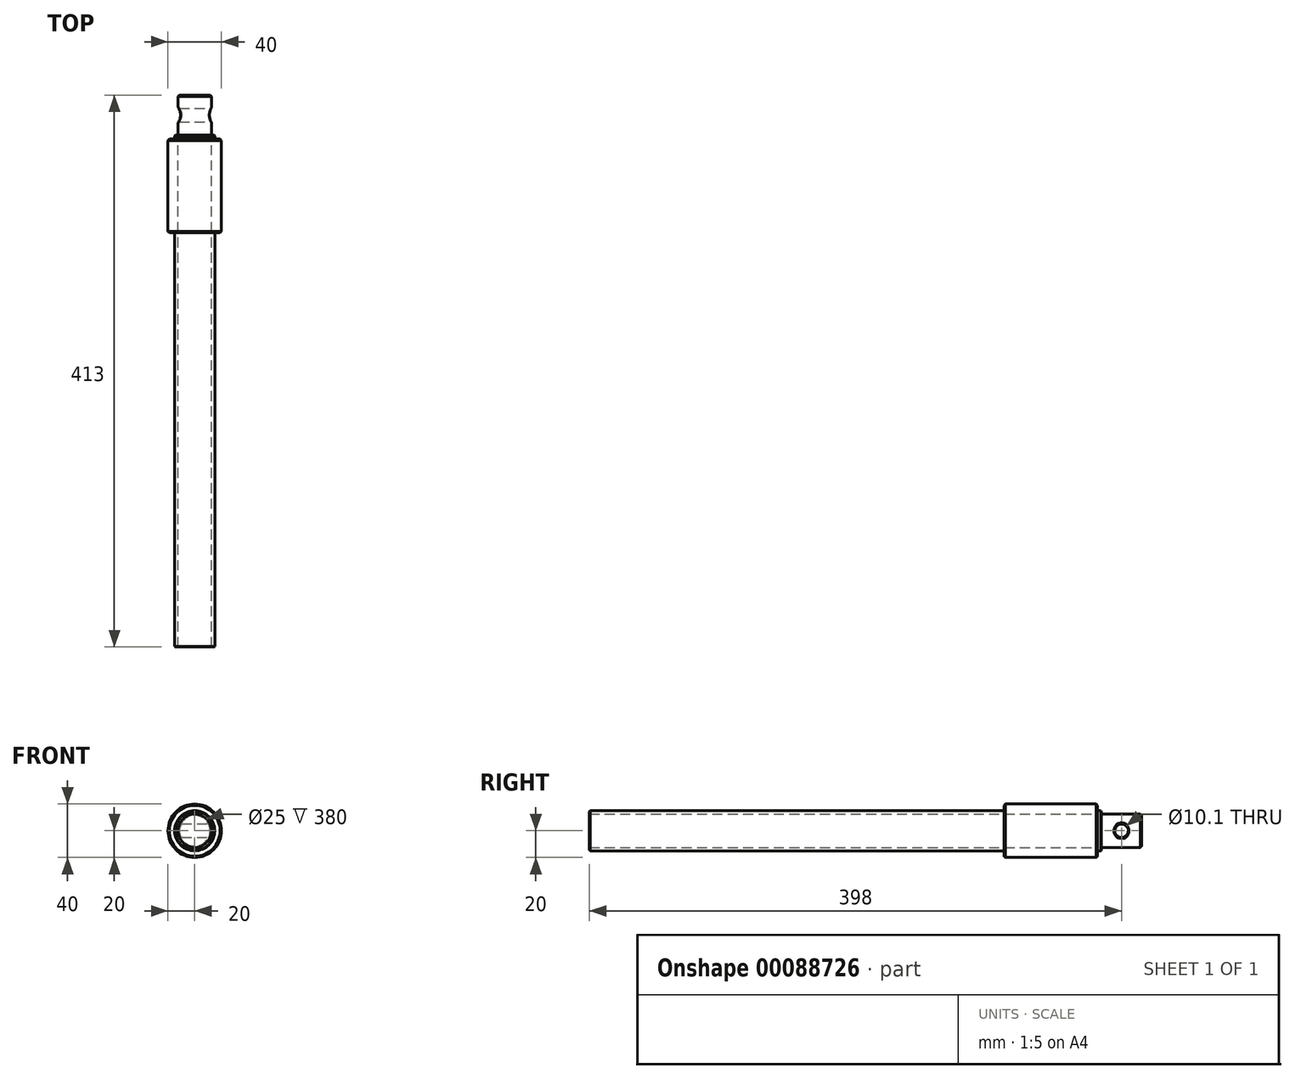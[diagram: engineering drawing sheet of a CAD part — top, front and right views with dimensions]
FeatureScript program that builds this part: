
annotation { "Feature Type Name" : "Feature", "Feature Type Description" : "" }
export const myFeature = defineFeature(function(context is Context, id is Id, definition is map)
    precondition{}
    {
        {
            var Q0;
            Q0=qCreatedBy(makeId("Front.planeOp"),FACE);
            var sketch = newSketch(context, id + "F0", { "sketchPlane" : qUnion([Q0])});
            skCircle(sketch, "E0", {"center": v(0, 0) * mm, "radius": 20 * mm});
            skCircle(sketch, "E1", {"center": v(0, 0) * mm, "radius": 15 * mm});
            skCircle(sketch, "E2", {"center": v(0, 0) * mm, "radius": 12.5 * mm});
            skSolve(sketch);
        }
        {
            var Q0;
            Q0 = qSketchRegion(id + "F0", true);
            var Q1;
            Q1=makeQuery(id+"F0.imprint","IMPRINT",FACE,{"disambiguationData":[TD([[makeQuery(id+"F0.imprint","IMPRINT",EDGE,{"derivedFrom":sQuery(id+"F0.wireOp",EDGE,"E0")}),1.0]])]});
            extrude(context, id + "F1", {"entities" : qUnion([Q0, Q1]), "depth" : 70 * mm});
        }
        {
            var Q0;
            Q0=makeQuery(id+"F0.imprint","IMPRINT",FACE,{"disambiguationData":[TD([[makeQuery(id+"F0.imprint","IMPRINT",EDGE,{"derivedFrom":sQuery(id+"F0.wireOp",EDGE,"E1")}),1.0]])]});
            extrude(context, id + "F2", {"entities" : qUnion([Q0]), "operationType" : NewBodyOperationType.ADD, "depth" : 380 * mm});
        }
        {
            var Q0;
            Q0=makeQuery(id+"F0.imprint","IMPRINT",FACE,{"disambiguationData":[TD([[makeQuery(id+"F0.imprint","IMPRINT",EDGE,{"derivedFrom":sQuery(id+"F0.wireOp",EDGE,"E1")}),1.0]])]});
            extrude(context, id + "F3", {"entities" : qUnion([Q0]), "operationType" : NewBodyOperationType.ADD, "oppositeDirection" : true, "depth" : 3 * mm});
        }
        {
            var Q0;
            Q0=makeQuery(id+"F0.imprint","IMPRINT",FACE,{"disambiguationData":[TD([[makeQuery(id+"F0.imprint","IMPRINT",EDGE,{"derivedFrom":sQuery(id+"F0.wireOp",EDGE,"E2")}),1.0]])]});
            extrude(context, id + "F4", {"entities" : qUnion([Q0]), "operationType" : NewBodyOperationType.ADD, "oppositeDirection" : true, "depth" : 33 * mm});
        }
        {
            var Q0;
            Q0=qCreatedBy(makeId("Right.planeOp"),FACE);
            var sketch = newSketch(context, id + "F5", { "sketchPlane" : qUnion([Q0])});
            skCircle(sketch, "E3", {"center": v(18, 0) * mm, "radius": 5.05 * mm});
            skSolve(sketch);
        }
        {
            var Q0;
            Q0 = qSketchRegion(id + "F5", true);
            extrude(context, id + "F6", {"entities" : qUnion([Q0]), "operationType" : NewBodyOperationType.REMOVE, "oppositeDirection" : true, "depth" : 25 * mm, "symmetric" : true});
        }
        {
            var Q0;
            Q0=makeQuery(id+"F4.opExtrude","CAP_EDGE",EDGE,{"disambiguationData":[OSD([sQuery(id+"F0.wireOp",EDGE,"E2")])],"isStart":false});
            var Q1;
            Q1=makeQuery(id+"F6.boolean.opBoolean","INTERSECT",EDGE,{"disambiguationData":[OD(0.0)],"derivedFrom":[makeQuery(id+"F4.opExtrude","SWEPT_FACE",FACE,{"disambiguationData":[OSD([sQuery(id+"F0.wireOp",EDGE,"E2")])]}),makeQuery(id+"F6.opExtrude","SWEPT_FACE",FACE,{"disambiguationData":[OSD([sQuery(id+"F5.wireOp",EDGE,"E3")])]})]});
            var Q2;
            Q2=makeQuery(id+"F6.boolean.opBoolean","INTERSECT",EDGE,{"disambiguationData":[OD(1.0)],"derivedFrom":[makeQuery(id+"F4.opExtrude","SWEPT_FACE",FACE,{"disambiguationData":[OSD([sQuery(id+"F0.wireOp",EDGE,"E2")])]}),makeQuery(id+"F6.opExtrude","SWEPT_FACE",FACE,{"disambiguationData":[OSD([sQuery(id+"F5.wireOp",EDGE,"E3")])]})]});
            chamfer(context, id + "F7", {"entities" : qUnion([Q0, Q1, Q2]), "width" : 1 * mm, "tangentPropagation" : true});
        }
        {
            var Q0;
            Q0=makeQuery(id+"F3.opExtrude","CAP_EDGE",EDGE,{"disambiguationData":[OSD([sQuery(id+"F0.wireOp",EDGE,"E1")])],"isStart":false});
            chamfer(context, id + "F8", {"entities" : qUnion([Q0]), "width" : 0.5 * mm, "tangentPropagation" : true});
        }
        {
            var Q0;
            Q0=makeQuery(id+"F1.opExtrude","CAP_EDGE",EDGE,{"disambiguationData":[OSD([sQuery(id+"F0.wireOp",EDGE,"E0")])],"isStart":true});
            var Q1;
            Q1=makeQuery(id+"F1.opExtrude","CAP_EDGE",EDGE,{"disambiguationData":[OSD([sQuery(id+"F0.wireOp",EDGE,"E0")])],"isStart":false});
            chamfer(context, id + "F9", {"entities" : qUnion([Q0, Q1]), "width" : 1 * mm, "tangentPropagation" : true});
        }
        {
            var Q0;
            Q0=makeQuery(id+"F2.opExtrude","CAP_EDGE",EDGE,{"disambiguationData":[OSD([sQuery(id+"F0.wireOp",EDGE,"E1")])],"isStart":false});
            chamfer(context, id + "F10", {"entities" : qUnion([Q0]), "width" : 0.5 * mm, "tangentPropagation" : true});
        }
    });
